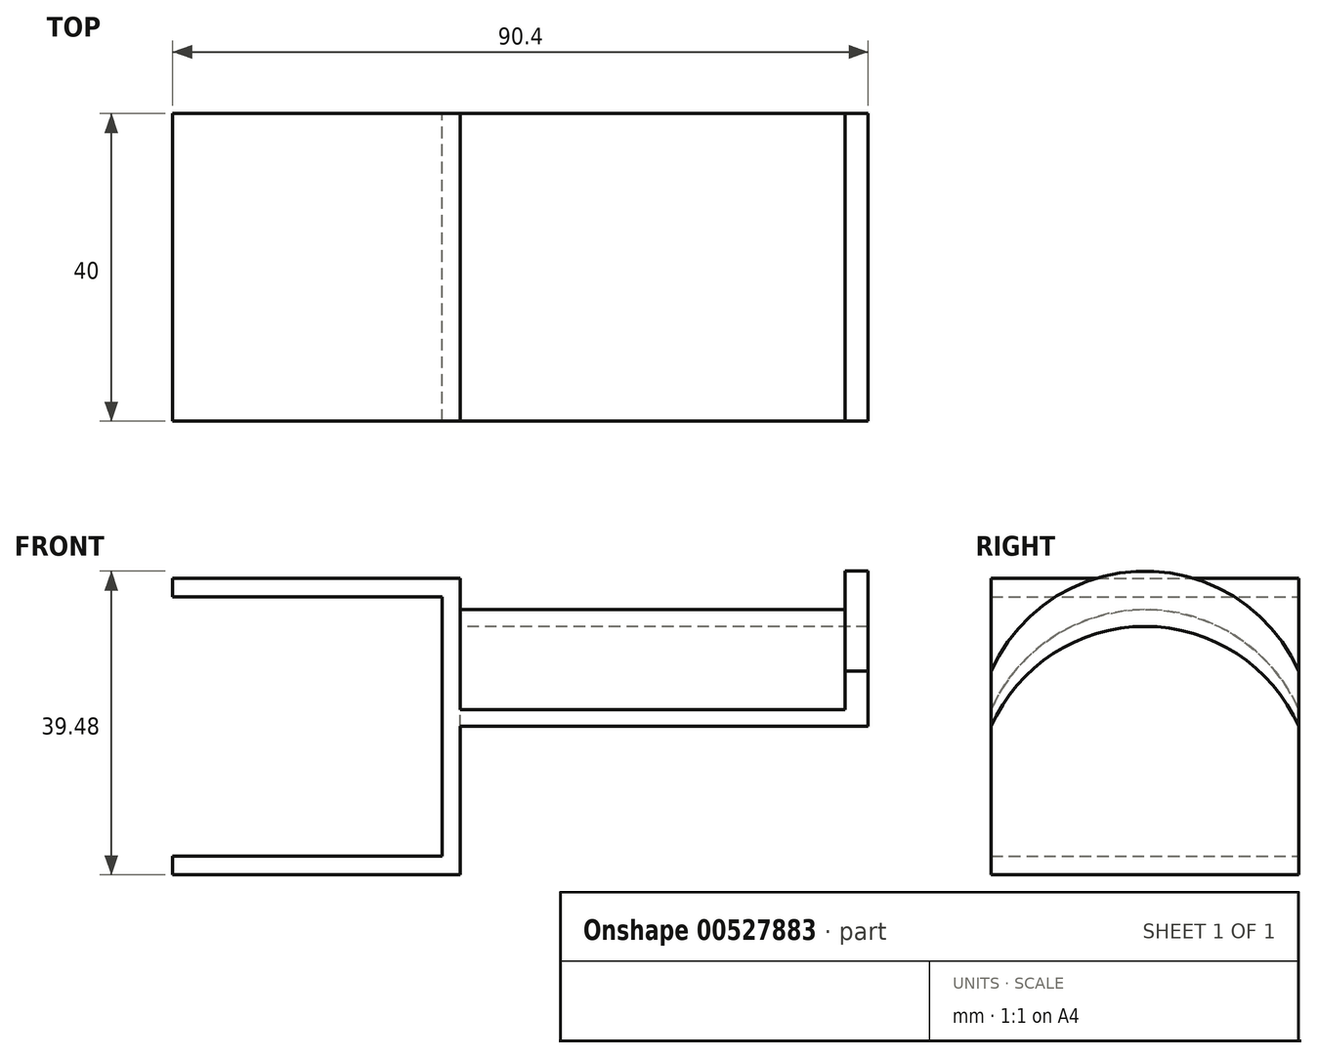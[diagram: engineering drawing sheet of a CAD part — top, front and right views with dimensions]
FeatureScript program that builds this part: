
annotation { "Feature Type Name" : "Feature", "Feature Type Description" : "" }
export const myFeature = defineFeature(function(context is Context, id is Id, definition is map)
    precondition{}
    {
        {
            var Q0;
            Q0=qCreatedBy(makeId("Front.planeOp"),FACE);
            var sketch = newSketch(context, id + "F0", { "sketchPlane" : qUnion([Q0])});
            skLineSegment(sketch, "E0", {"start": v(0, 38.55) * mm, "end": v(37.4, 38.55) * mm});
            skLineSegment(sketch, "E1", {"start": v(37.4, 38.55) * mm, "end": v(37.4, 0) * mm});
            skLineSegment(sketch, "E2", {"start": v(37.4, 0) * mm, "end": v(0, 0) * mm});
            skLineSegment(sketch, "E3", {"start": v(0, 0) * mm, "end": v(0, 2.4) * mm});
            skLineSegment(sketch, "E4", {"start": v(0, 2.4) * mm, "end": v(35, 2.4) * mm});
            skLineSegment(sketch, "E5", {"start": v(35, 2.4) * mm, "end": v(35, 36.15) * mm});
            skLineSegment(sketch, "E6", {"start": v(35, 36.15) * mm, "end": v(0, 36.15) * mm});
            skLineSegment(sketch, "E7", {"start": v(0, 36.15) * mm, "end": v(0, 38.55) * mm});
            skLineSegment(sketch, "E8", {"start": v(35, 3.71) * mm, "end": v(37.4, 3.71) * mm, "construction": true});
            skSolve(sketch);
        }
        {
            var Q0;
            Q0 = qSketchRegion(id + "F0", true);
            extrude(context, id + "F1", {"entities" : qUnion([Q0]), "endBound" : BoundingType.SYMMETRIC, "depth" : 40 * mm, "offsetDistance" : 25 * mm});
        }
        {
            var Q0;
            Q0=makeQuery(id+"F1.opExtrude","SWEPT_FACE",FACE,{"disambiguationData":[OSD([sQuery(id+"F0.wireOp",EDGE,"E1")])]});
            var sketch = newSketch(context, id + "F2", { "sketchPlane" : qUnion([Q0])});
            skArc(sketch, "E9", {"start": v(20, 19.27) * mm, "mid": v(0, 32.28) * mm, "end": v(-20, 19.28) * mm});
            skArc(sketch, "E10", {"start": v(20, 21.48) * mm, "mid": v(0, 34.48) * mm, "end": v(-20, 21.48) * mm});
            skLineSegment(sketch, "E11", {"start": v(-20, 19.28) * mm, "end": v(-20, 21.47) * mm});
            skLineSegment(sketch, "E12", {"start": v(20, 21.47) * mm, "end": v(20, 19.27) * mm});
            skSolve(sketch);
        }
        {
            var Q0;
            Q0 = qSketchRegion(id + "F2", true);
            extrude(context, id + "F3", {"entities" : qUnion([Q0]), "operationType" : NewBodyOperationType.ADD, "depth" : 53 * mm, "offsetDistance" : 25 * mm});
        }
        {
            var Q0;
            Q0=makeQuery(id+"F3.boolean.opBoolean","MERGE",FACE,{"derivedFrom":[makeQuery(id+"F1.opExtrude","CAP_FACE",FACE,{"disambiguationData":[OSD([sQuery(id+"F0.wireOp",EDGE,"E0"),sQuery(id+"F0.wireOp",EDGE,"E1"),sQuery(id+"F0.wireOp",EDGE,"E2"),sQuery(id+"F0.wireOp",EDGE,"E3"),sQuery(id+"F0.wireOp",EDGE,"E4"),sQuery(id+"F0.wireOp",EDGE,"E5"),sQuery(id+"F0.wireOp",EDGE,"E6"),sQuery(id+"F0.wireOp",EDGE,"E7")])],"isStart":false}),makeQuery(id+"F3.opExtrude","SWEPT_FACE",FACE,{"disambiguationData":[OSD([sQuery(id+"F2.wireOp",EDGE,"E11")])]})]});
            var sketch = newSketch(context, id + "F4", { "sketchPlane" : qUnion([Q0])});
            skLineSegment(sketch, "E13.bottom", {"start": v(90.4, 21.48) * mm, "end": v(87.4, 21.48) * mm});
            skLineSegment(sketch, "E13.top", {"start": v(90.4, 26.48) * mm, "end": v(87.4, 26.48) * mm});
            skLineSegment(sketch, "E13.left", {"start": v(90.4, 21.48) * mm, "end": v(90.4, 26.48) * mm});
            skLineSegment(sketch, "E13.right", {"start": v(87.4, 21.48) * mm, "end": v(87.4, 26.48) * mm});
            skSolve(sketch);
        }
        {
            var Q0;
            Q0=makeQuery(id+"F4.imprint","IMPRINT",FACE,{"disambiguationData":[TD([[makeQuery(id+"F4.imprint","IMPRINT",EDGE,{"derivedFrom":sQuery(id+"F4.wireOp",EDGE,"E13.bottom")}),-1.0]])]});
            var Q1;
            Q1=makeQuery(id+"F3.opExtrude","CAP_EDGE",EDGE,{"disambiguationData":[OSD([sQuery(id+"F2.wireOp",EDGE,"E10")])],"isStart":false});
            sweep(context, id + "F5", {"operationType" : NewBodyOperationType.ADD, "profiles" : qUnion([Q0]), "path" : qUnion([Q1]), "keepProfileOrientation" : true});
        }
    });
